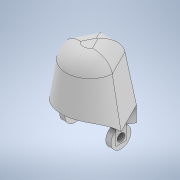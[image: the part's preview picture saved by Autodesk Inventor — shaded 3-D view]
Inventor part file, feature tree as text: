
AUTODESK INVENTOR PART (.ipt)
format: ipt  version: 2022 (Build 260153000, 153)  size: 333,824 bytes
history: native  units: mm
features: sketch x11, extrude x7, other x5, loft x1, fillet x1, shell x1
ambient origin geometry x8: Origin, YZ Plane, XZ Plane, XY Plane, X Axis, Y Axis, Z Axis, Center Point
bodies: Body1 (feature_tree)
feature tree (26):
  sketch  "스케치2"
  other  "작업 평면2"
  sketch  "스케치3"
  other  "작업 평면4"
  loft  "로프트1"
  fillet  "모깎기1"  Radius=5.0mm
  sketch  "스케치5"
  extrude  "돌출2"  Depth=20.0mm
  other  "작업 평면5"
  sketch  "스케치7"
  sketch  "스케치11"
  shell  "쉘2"  Thickness=-20.0mm
  sketch  "스케치16"
  extrude  "돌출10"  TaperAngle=0.0deg  [1 undecoded]
  sketch  "스케치20"
  extrude  "돌출13"  TaperAngle=0.0deg  [1 undecoded]
  sketch  "스케치22"
  other  "작업 평면8"
  extrude  "돌출17"  TaperAngle=0.0deg  [1 undecoded]
  extrude  "돌출18"  Depth=5.5mm
  extrude  "돌출19"  Depth=43.5mm TaperAngle=0.0deg
  extrude  "돌출20"  TaperAngle=0.0deg  [1 undecoded]
  other  "작업 평면3"
  sketch  "스케치4"
  sketch  "스케치6"
  sketch  "스케치21"
note: 4 required parameter values undecoded (feature->parameter linkage not recoverable at this tier; creation-order binding heuristic only, values carry confidence <= 0.55)
